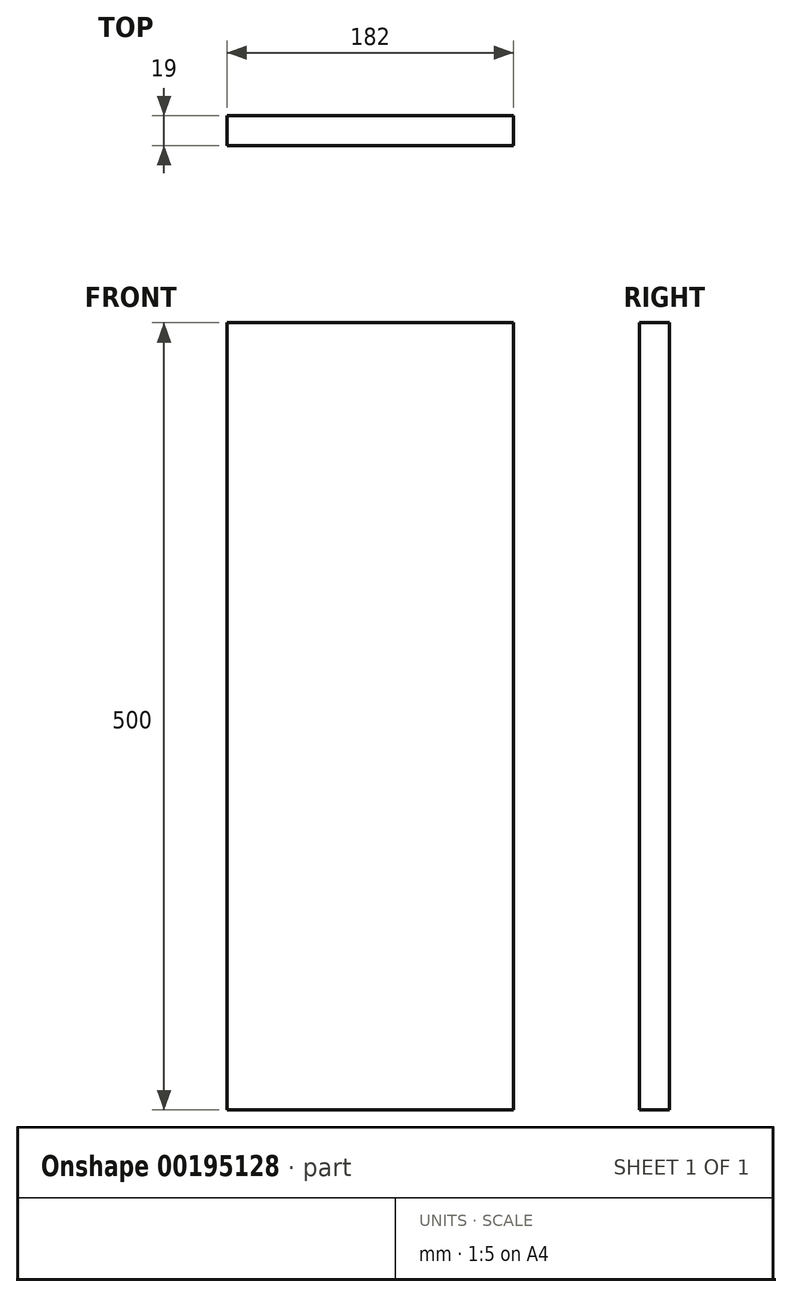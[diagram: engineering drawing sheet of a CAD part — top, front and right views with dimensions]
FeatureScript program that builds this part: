
annotation { "Feature Type Name" : "Feature", "Feature Type Description" : "" }
export const myFeature = defineFeature(function(context is Context, id is Id, definition is map)
    precondition{}
    {
        {
            var Q0;
            Q0=qCreatedBy(makeId("Front.planeOp"),FACE);
            var sketch = newSketch(context, id + "F0", { "sketchPlane" : qUnion([Q0])});
            skLineSegment(sketch, "E0.bottom", {"start": v(-91, 250) * mm, "end": v(91, 250) * mm});
            skLineSegment(sketch, "E0.top", {"start": v(-91, -250) * mm, "end": v(91, -250) * mm});
            skLineSegment(sketch, "E0.left", {"start": v(-91, 250) * mm, "end": v(-91, -250) * mm});
            skLineSegment(sketch, "E0.right", {"start": v(91, 250) * mm, "end": v(91, -250) * mm});
            skSolve(sketch);
        }
        {
            var Q0;
            Q0=makeQuery(id+"F0.imprint","IMPRINT",FACE,{"disambiguationData":[TD([[makeQuery(id+"F0.imprint","IMPRINT",EDGE,{"derivedFrom":sQuery(id+"F0.wireOp",EDGE,"E0.bottom")}),-1.0]])]});
            extrude(context, id + "F1", {"entities" : qUnion([Q0]), "depth" : 19 * mm});
        }
    });
